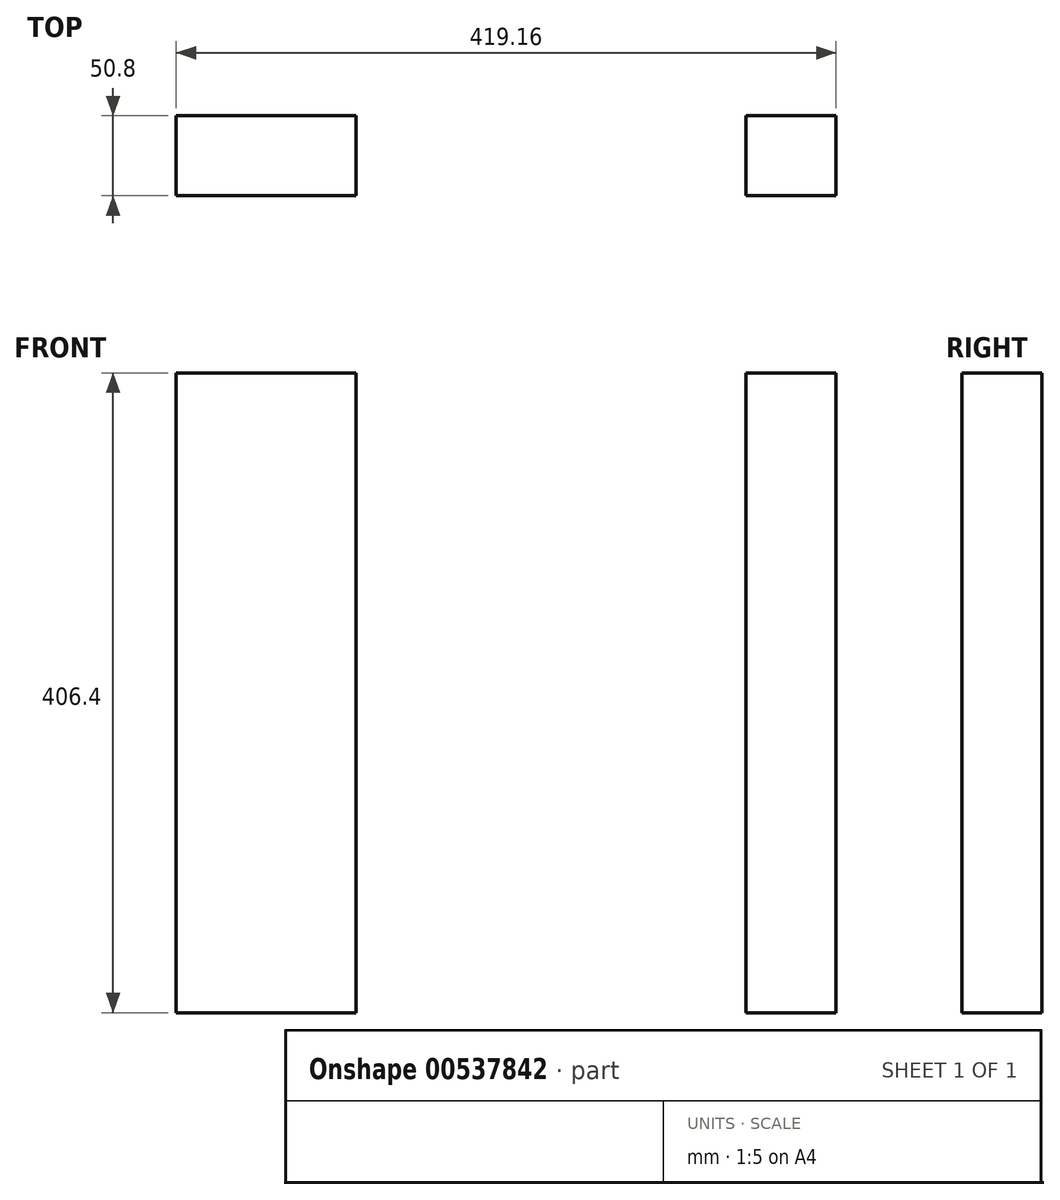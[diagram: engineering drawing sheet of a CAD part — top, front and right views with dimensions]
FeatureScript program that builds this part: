
annotation { "Feature Type Name" : "Feature", "Feature Type Description" : "" }
export const myFeature = defineFeature(function(context is Context, id is Id, definition is map)
    precondition{}
    {
        {
            var Q0;
            Q0=qCreatedBy(makeId("Top.planeOp"),FACE);
            var sketch = newSketch(context, id + "F0", { "sketchPlane" : qUnion([Q0])});
            skLineSegment(sketch, "E0.bottom", {"start": v(0, 0) * mm, "end": v(57.18, 0) * mm});
            skLineSegment(sketch, "E0.top", {"start": v(0, 50.8) * mm, "end": v(57.18, 50.8) * mm});
            skLineSegment(sketch, "E0.left", {"start": v(0, 0) * mm, "end": v(0, 50.8) * mm});
            skLineSegment(sketch, "E0.right", {"start": v(57.18, 0) * mm, "end": v(57.18, 50.8) * mm});
            skLineSegment(sketch, "E1", {"start": v(0, 50.8) * mm, "end": v(-304.8, 50.8) * mm});
            skLineSegment(sketch, "E2", {"start": v(-152.4, 50.8) * mm, "end": v(-152.4, -87.38) * mm});
            skLineSegment(sketch, "E3.MirrorCS", {"start": v(-304.8, 0) * mm, "end": v(-304.8, 50.8) * mm});
            skLineSegment(sketch, "E4.MirrorCS", {"start": v(-304.8, 0) * mm, "end": v(-361.98, 0) * mm});
            skLineSegment(sketch, "E5.MirrorCS", {"start": v(-361.98, 0) * mm, "end": v(-361.98, 50.8) * mm});
            skLineSegment(sketch, "E6.MirrorCS", {"start": v(-304.8, 50.8) * mm, "end": v(-361.98, 50.8) * mm});
            skLineSegment(sketch, "E7.MirrorCS", {"start": v(-247.62, 0) * mm, "end": v(-247.62, 50.8) * mm});
            skLineSegment(sketch, "E8.MirrorCS", {"start": v(-304.8, 0) * mm, "end": v(-247.62, 0) * mm});
            skLineSegment(sketch, "E9.MirrorCS", {"start": v(-457.2, 50.8) * mm, "end": v(-457.2, -87.38) * mm});
            skSolve(sketch);
        }
        {
            var Q0;
            Q0 = qSketchRegion(id + "F0", true);
            extrude(context, id + "F1", {"entities" : qUnion([Q0]), "depth" : 406.4 * mm, "offsetDistance" : 25.4 * mm});
        }
    });
